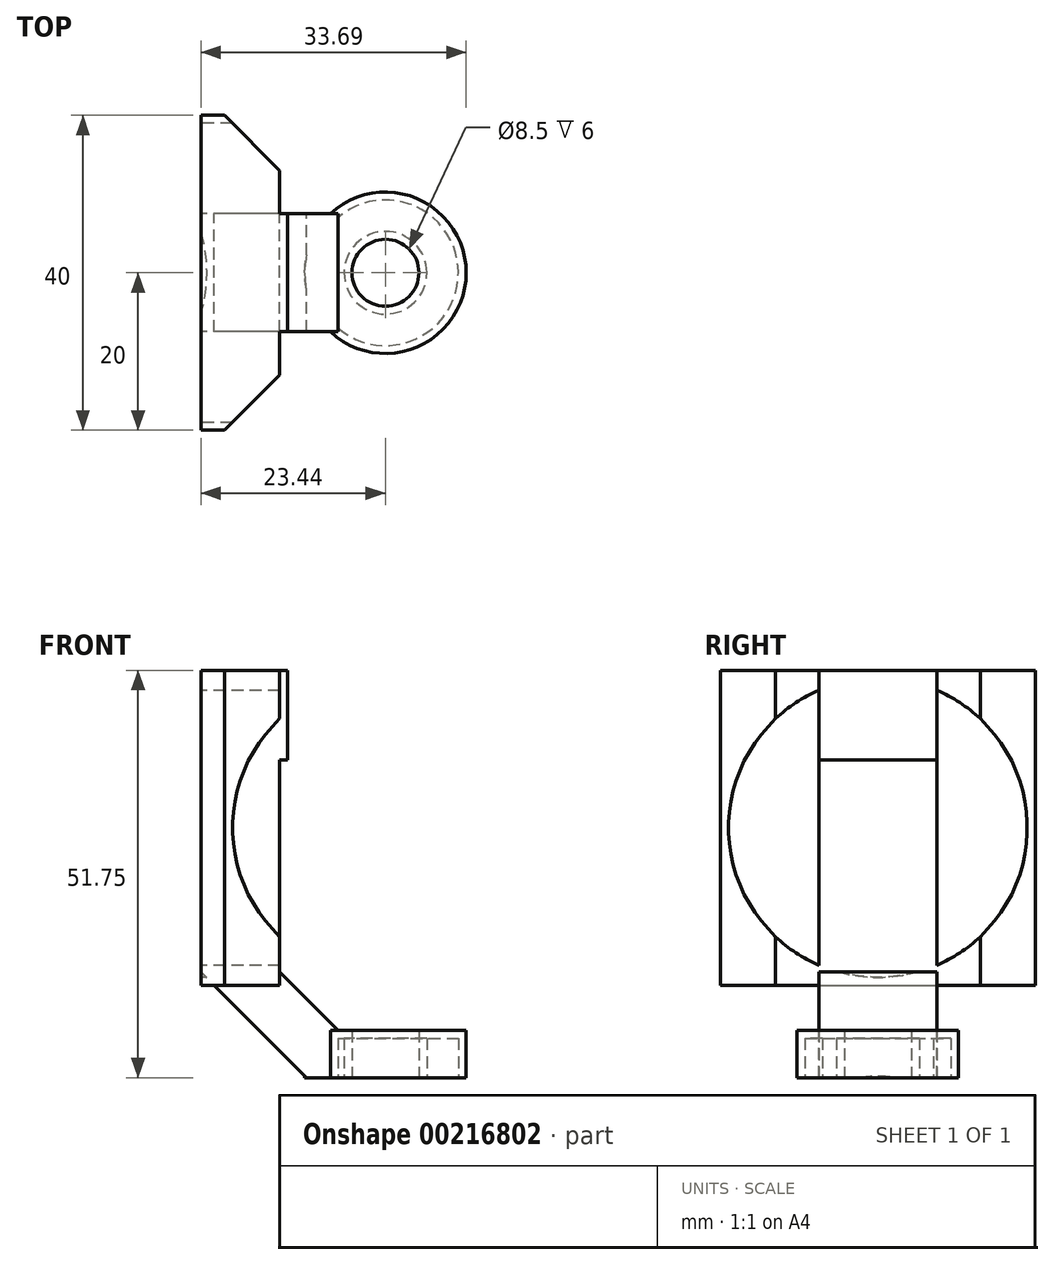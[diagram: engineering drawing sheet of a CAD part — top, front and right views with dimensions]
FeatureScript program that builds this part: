
annotation { "Feature Type Name" : "Feature", "Feature Type Description" : "" }
export const myFeature = defineFeature(function(context is Context, id is Id, definition is map)
    precondition{}
    {
        {
            var Q0;
            Q0=qCreatedBy(makeId("Top.planeOp"),FACE);
            var sketch = newSketch(context, id + "F0", { "sketchPlane" : qUnion([Q0])});
            skCircle(sketch, "E0", {"center": v(0, 0) * mm, "radius": 4.25 * mm});
            skCircle(sketch, "E1.0", {"center": v(0, 0) * mm, "radius": 10.25 * mm});
            skLineSegment(sketch, "E2", {"start": v(0, 10.25) * mm, "end": v(0, -10.25) * mm, "construction": true});
            skSolve(sketch);
        }
        {
            var Q0;
            Q0=makeQuery(id+"F0.imprint","IMPRINT",FACE,{"disambiguationData":[TD([[makeQuery(id+"F0.imprint","IMPRINT",EDGE,{"derivedFrom":sQuery(id+"F0.wireOp",EDGE,"E0")}),-1.0]])]});
            var Q1;
            Q1=makeQuery(id+"F0.imprint","IMPRINT",FACE,{"disambiguationData":[TD([[makeQuery(id+"F0.imprint","IMPRINT",EDGE,{"derivedFrom":sQuery(id+"F0.wireOp",EDGE,"e5409c65-e9f0-44f2-ad46-98301513d94e.0")}),1.0]])]});
            var Q2;
            Q2=makeQuery(id+"F0.imprint","IMPRINT",FACE,{"disambiguationData":[TD([[makeQuery(id+"F0.imprint","IMPRINT",EDGE,{"derivedFrom":sQuery(id+"F0.wireOp",EDGE,"E1.0")}),1.0]])]});
            var Q3;
            {var subQ1=sQuery(id+"F0.wireOp",EDGE,"I8Fj6QRq-puFd-Nm9C-Qs67-yFoKpzJXSVMP.bottom");Q3=makeQuery(id+"F0.imprint","IMPRINT",FACE,{"disambiguationData":[TD([[makeQuery(id+"F0.imprint","IMPRINT",EDGE,{"derivedFrom":subQ1}),-1.0]])]});}
            extrude(context, id + "F1", {"entities" : qUnion([Q0, Q1, Q2, Q3]), "depth" : 6 * mm});
        }
        {
            var Q0;
            Q0=makeQuery(id+"F1.opExtrude","CAP_FACE",FACE,{"disambiguationData":[OSD([sQuery(id+"F0.wireOp",EDGE,"E0"),sQuery(id+"F0.wireOp",EDGE,"E1.0")])],"isStart":true});
            shell(context, id + "F2", {"entities" : qUnion([Q0]), "thickness" : 1 * mm});
        }
        {
            var Q0;
            Q0=qCreatedBy(makeId("Front.planeOp"),FACE);
            var sketch = newSketch(context, id + "F3", { "sketchPlane" : qUnion([Q0])});
            skLineSegment(sketch, "E3", {"start": v(-23.44, 13.44) * mm, "end": v(-23.44, 51.75) * mm});
            skLineSegment(sketch, "E4", {"start": v(-23.44, 51.75) * mm, "end": v(-12.44, 51.75) * mm});
            skLineSegment(sketch, "E5", {"start": v(-12.44, 51.75) * mm, "end": v(-12.44, 40.35) * mm});
            skLineSegment(sketch, "E6", {"start": v(-12.44, 40.35) * mm, "end": v(-13.44, 40.35) * mm});
            skLineSegment(sketch, "E7", {"start": v(-13.44, 40.35) * mm, "end": v(-13.44, 13.44) * mm});
            skLineSegment(sketch, "E8", {"start": v(-6, 6) * mm, "end": v(-13.44, 13.44) * mm});
            skLineSegment(sketch, "E9", {"start": v(-6, 6) * mm, "end": v(0, 6) * mm});
            skLineSegment(sketch, "E10", {"start": v(0, 6) * mm, "end": v(0, 0) * mm});
            skLineSegment(sketch, "E11", {"start": v(0, 0) * mm, "end": v(-10, 0) * mm});
            skLineSegment(sketch, "E12", {"start": v(-10, 0) * mm, "end": v(-23.44, 13.44) * mm});
            skLineSegment(sketch, "E13", {"start": v(-6, 6) * mm, "end": v(-6, 0) * mm});
            skSolve(sketch);
        }
        {
            var Q0;
            Q0=makeQuery(id+"F3.imprint","IMPRINT",FACE,{"disambiguationData":[TD([[makeQuery(id+"F3.imprint","IMPRINT",EDGE,{"derivedFrom":sQuery(id+"F3.wireOp",EDGE,"E3")}),-1.0]])]});
            extrude(context, id + "F4", {"entities" : qUnion([Q0]), "operationType" : NewBodyOperationType.ADD, "endBound" : BoundingType.SYMMETRIC, "depth" : 15 * mm});
        }
        {
            var Q0;
            Q0=makeQuery(id+"F4.opExtrude","SWEPT_FACE",FACE,{"disambiguationData":[OSD([sQuery(id+"F3.wireOp",EDGE,"E3")])]});
            var sketch = newSketch(context, id + "F5", { "sketchPlane" : qUnion([Q0])});
            skLineSegment(sketch, "E14.bottom", {"start": v(20, 51.75) * mm, "end": v(-20, 51.75) * mm});
            skLineSegment(sketch, "E14.top", {"start": v(20, 11.75) * mm, "end": v(-20, 11.75) * mm});
            skLineSegment(sketch, "E14.left", {"start": v(20, 51.75) * mm, "end": v(20, 11.75) * mm});
            skLineSegment(sketch, "E14.right", {"start": v(-20, 51.75) * mm, "end": v(-20, 11.75) * mm});
            skPoint(sketch, "E14.middle", {"position": v(0, 31.75) * mm});
            skCircle(sketch, "E15", {"center": v(0, 31.75) * mm, "radius": 19 * mm});
            skSolve(sketch);
        }
        {
            var Q0;
            {var subQ3=sQuery(id+"F5.wireOp",EDGE,"E14.left");Q0=makeQuery(id+"F5.imprint","IMPRINT",FACE,{"disambiguationData":[TD([[makeQuery(id+"F5.imprint","IMPRINT",EDGE,{"derivedFrom":subQ3}),-1.0]])]});}
            var Q1;
            {var subQ3=sQuery(id+"F5.wireOp",EDGE,"E14.right");Q1=makeQuery(id+"F5.imprint","IMPRINT",FACE,{"disambiguationData":[TD([[makeQuery(id+"F5.imprint","IMPRINT",EDGE,{"derivedFrom":subQ3}),1.0]])]});}
            var Q2;
            {var subQ0=sQuery(id+"F5.wireOp",EDGE,"E15");var subQ1=makeQuery(id+"F4.opExtrude","CAP_EDGE",EDGE,{"disambiguationData":[OSD([sQuery(id+"F3.wireOp",EDGE,"E3")])],"isStart":false});var subQ2=makeQuery(id+"F5.imprint","INTERSECT",VERTEX,{"disambiguationData":[OD(0.0)],"derivedFrom":[subQ1,subQ0]});Q2=makeQuery(id+"F5.imprint","IMPRINT",FACE,{"disambiguationData":[TD([[makeQuery(id+"F5.imprint","IMPRINT",EDGE,{"disambiguationData":[TD([[subQ2,1.0]])],"derivedFrom":subQ0}),1.0]])]});}
            var Q3;
            {var subQ0=sQuery(id+"F5.wireOp",EDGE,"E15");var subQ1=makeQuery(id+"F4.opExtrude","CAP_EDGE",EDGE,{"disambiguationData":[OSD([sQuery(id+"F3.wireOp",EDGE,"E3")])],"isStart":true});var subQ2=makeQuery(id+"F5.imprint","INTERSECT",VERTEX,{"disambiguationData":[OD(0.0)],"derivedFrom":[subQ1,subQ0]});Q3=makeQuery(id+"F5.imprint","IMPRINT",FACE,{"disambiguationData":[TD([[makeQuery(id+"F5.imprint","IMPRINT",EDGE,{"disambiguationData":[TD([[subQ2,-1.0]])],"derivedFrom":subQ0}),1.0]])]});}
            var Q4;
            Q4=makeQuery(id+"F4.opExtrude","SWEPT_FACE",FACE,{"disambiguationData":[OSD([sQuery(id+"F3.wireOp",EDGE,"E7")])]});
            extrude(context, id + "F6", {"entities" : qUnion([Q0, Q1, Q2, Q3]), "operationType" : NewBodyOperationType.ADD, "endBound" : BoundingType.UP_TO_SURFACE, "oppositeDirection" : true, "endBoundEntityFace" : qUnion([Q4]), "depth" : 25 * mm});
        }
        {
            var Q0;
            Q0=makeQuery(id+"F6.opExtrude","CAP_EDGE",EDGE,{"disambiguationData":[OSD([sQuery(id+"F5.wireOp",EDGE,"E14.left")])],"isStart":false});
            var Q1;
            Q1=makeQuery(id+"F6.opExtrude","CAP_EDGE",EDGE,{"disambiguationData":[OSD([sQuery(id+"F5.wireOp",EDGE,"E14.right")])],"isStart":false});
            chamfer(context, id + "F7", {"entities" : qUnion([Q0, Q1]), "width" : 7 * mm, "tangentPropagation" : true});
        }
    });
